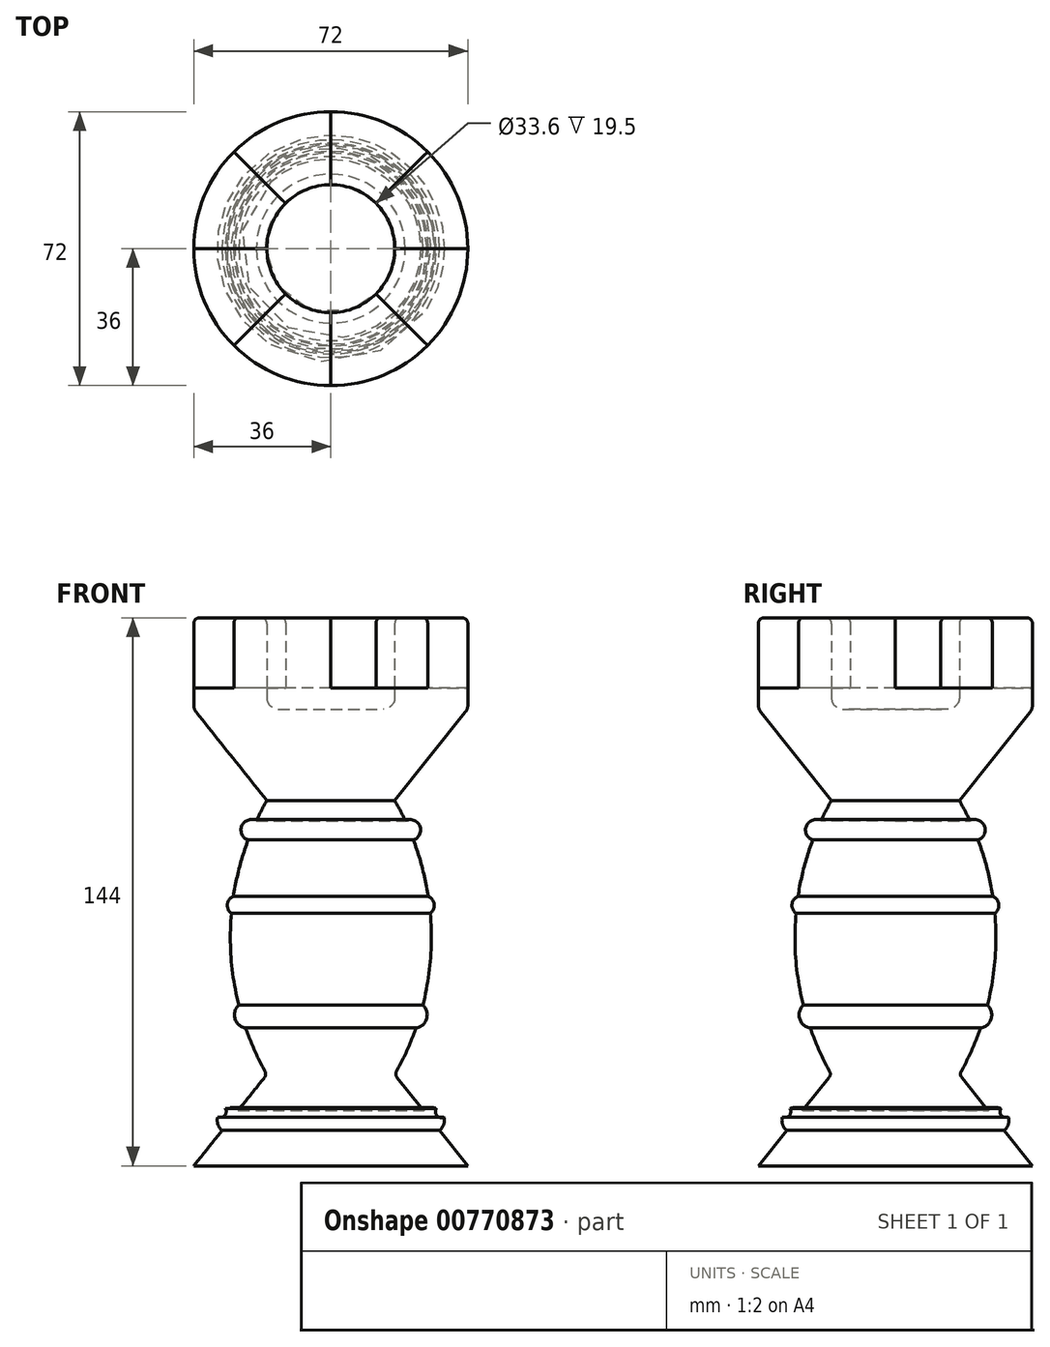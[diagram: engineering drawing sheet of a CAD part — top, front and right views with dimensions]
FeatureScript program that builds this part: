
annotation { "Feature Type Name" : "Feature", "Feature Type Description" : "" }
export const myFeature = defineFeature(function(context is Context, id is Id, definition is map)
    precondition{}
    {
        {
            var Q0;
            Q0=qCreatedBy(makeId("Right.planeOp"),FACE);
            var sketch = newSketch(context, id + "F0", { "sketchPlane" : qUnion([Q0])});
            skLineSegment(sketch, "E0", {"start": v(-36, -74.45) * mm, "end": v(-17.43, -51.25) * mm});
            skLineSegment(sketch, "E1", {"start": v(-35.34, 44.72) * mm, "end": v(-16.8, 21.55) * mm});
            skLineSegment(sketch, "E2", {"start": v(-33, 69.55) * mm, "end": v(-19.8, 69.55) * mm});
            skLineSegment(sketch, "E3", {"start": v(-36, 66.55) * mm, "end": v(-36, 46.6) * mm});
            skLineSegment(sketch, "E4", {"start": v(-16.8, 48.55) * mm, "end": v(-16.8, 66.55) * mm});
            skArc(sketch, "E5", {"start": v(-16.8, 21.55) * mm, "mid": v(-26.4, -13.95) * mm, "end": v(-17.3, -49.58) * mm});
            skLineSegment(sketch, "E6", {"start": v(0, -74.45) * mm, "end": v(-36, -74.45) * mm});
            skLineSegment(sketch, "E7", {"start": v(-13.8, 45.55) * mm, "end": v(0, 45.55) * mm});
            skArc(sketch, "E8", {"start": v(-16.8, 48.55) * mm, "mid": v(-15.92, 46.43) * mm, "end": v(-13.8, 45.55) * mm});
            skArc(sketch, "E9", {"start": v(-36, 46.6) * mm, "mid": v(-35.83, 45.6) * mm, "end": v(-35.34, 44.72) * mm});
            skLineSegment(sketch, "E10", {"start": v(-33, 69.55) * mm, "end": v(-34.5, 69.55) * mm});
            skLineSegment(sketch, "E11", {"start": v(-36, 66.55) * mm, "end": v(-36, 68.05) * mm});
            skLineSegment(sketch, "E12", {"start": v(-19.8, 69.55) * mm, "end": v(-18.3, 69.55) * mm});
            skLineSegment(sketch, "E13", {"start": v(-16.8, 66.55) * mm, "end": v(-16.8, 68.05) * mm});
            skArc(sketch, "E14", {"start": v(-34.5, 69.55) * mm, "mid": v(-35.56, 69.1) * mm, "end": v(-36, 68.05) * mm});
            skArc(sketch, "E15", {"start": v(-16.8, 68.05) * mm, "mid": v(-17.24, 69.1) * mm, "end": v(-18.3, 69.55) * mm});
            skArc(sketch, "E16", {"start": v(-17.43, -51.25) * mm, "mid": v(-17.11, -50.43) * mm, "end": v(-17.3, -49.58) * mm});
            skLineSegment(sketch, "E17", {"start": v(0, -74.45) * mm, "end": v(0, 45.55) * mm});
            skSolve(sketch);
        }
        {
            var Q0;
            Q0=makeQuery(id+"F0.imprint","IMPRINT",FACE,{"disambiguationData":[TD([[makeQuery(id+"F0.imprint","IMPRINT",EDGE,{"derivedFrom":sQuery(id+"F0.wireOp",EDGE,"E0")}),-1.0]])]});
            var Q1;
            Q1=sQuery(id+"F0.wireOp",EDGE,"E17");
            revolve(context, id + "F1", {"surfaceOperationType" : NewSurfaceOperationType.NEW, "entities" : qUnion([Q0]), "axis" : qUnion([Q1]), "revolveType" : RevolveType.FULL});
        }
        {
            var Q0;
            Q0=makeQuery(id+"F1.opRevolve","SWEPT_FACE",FACE,{"disambiguationData":[OSD([sQuery(id+"F0.wireOp",EDGE,"E2"),sQuery(id+"F0.wireOp",EDGE,"E10"),sQuery(id+"F0.wireOp",EDGE,"E12")])]});
            var sketch = newSketch(context, id + "F2", { "sketchPlane" : qUnion([Q0])});
            skLineSegment(sketch, "E18", {"start": v(0, 0) * mm, "end": v(0, 45.62) * mm});
            skLineSegment(sketch, "E19", {"start": v(0, 0) * mm, "end": v(59.77, 0) * mm});
            skLineSegment(sketch, "E20", {"start": v(0, 0) * mm, "end": v(0, -52.46) * mm});
            skLineSegment(sketch, "E21", {"start": v(0, 0) * mm, "end": v(-50.81, 0) * mm});
            skLineSegment(sketch, "E22", {"start": v(0, 0) * mm, "end": v(-38.32, 38.32) * mm});
            skLineSegment(sketch, "E23", {"start": v(0, 0) * mm, "end": v(37.23, 37.23) * mm});
            skLineSegment(sketch, "E24", {"start": v(0, 0) * mm, "end": v(42.66, -42.66) * mm});
            skLineSegment(sketch, "E25", {"start": v(0, 0) * mm, "end": v(-29.95, -29.95) * mm});
            skLineSegment(sketch, "E26", {"start": v(-38.32, 38.32) * mm, "end": v(0, 45.62) * mm});
            skLineSegment(sketch, "E27", {"start": v(37.23, 37.23) * mm, "end": v(59.77, 0) * mm});
            skLineSegment(sketch, "E28", {"start": v(42.66, -42.66) * mm, "end": v(0, -52.46) * mm});
            skLineSegment(sketch, "E29", {"start": v(-29.95, -29.95) * mm, "end": v(-50.81, 0) * mm});
            skSolve(sketch);
        }
        {
            var Q0;
            Q0=qSketchRegion(id+"F2",true);
            extrude(context, id + "F3", {"entities" : qUnion([Q0]), "operationType" : NewBodyOperationType.REMOVE, "oppositeDirection" : true, "depth" : 18.4 * mm, "offsetDistance" : 25 * mm});
        }
        {
            var Q0;
            Q0=qCreatedBy(makeId("Front.planeOp"),FACE);
            var sketch = newSketch(context, id + "F4", { "sketchPlane" : qUnion([Q0])});
            skCircle(sketch, "E30", {"center": v(26.48, -62.5) * mm, "radius": 3.35 * mm});
            skSolve(sketch);
        }
        {
            var Q0;
            Q0=qSketchRegion(id+"F4",true);
            var Q1;
            Q1=makeQuery(id+"F1.opRevolve","SWEPT_FACE",FACE,{"disambiguationData":[OSD([sQuery(id+"F0.wireOp",EDGE,"E0")])]});
            revolve(context, id + "F5", {"operationType" : NewBodyOperationType.ADD, "surfaceOperationType" : NewSurfaceOperationType.NEW, "entities" : qUnion([Q0]), "axis" : qUnion([Q1]), "revolveType" : RevolveType.FULL});
        }
        {
            var Q0;
            Q0=qCreatedBy(makeId("Front.planeOp"),FACE);
            var sketch = newSketch(context, id + "F6", { "sketchPlane" : qUnion([Q0])});
            skCircle(sketch, "E31", {"center": v(29.08, -60.2) * mm, "radius": 1.6 * mm});
            skSolve(sketch);
        }
        {
            var Q0;
            Q0=qSketchRegion(id+"F6",true);
            var Q1;
            Q1=makeQuery(id+"F5.opRevolve","SWEPT_FACE",FACE,{"disambiguationData":[OSD([sQuery(id+"F4.wireOp",EDGE,"E30")])]});
            revolve(context, id + "F7", {"operationType" : NewBodyOperationType.REMOVE, "surfaceOperationType" : NewSurfaceOperationType.NEW, "entities" : qUnion([Q0]), "axis" : qUnion([Q1]), "revolveType" : RevolveType.FULL, "oppositeDirection" : true});
        }
        {
            var Q0;
            Q0=qCreatedBy(makeId("Front.planeOp"),FACE);
            var sketch = newSketch(context, id + "F8", { "sketchPlane" : qUnion([Q0])});
            skCircle(sketch, "E32", {"center": v(20.87, 13.8) * mm, "radius": 2.75 * mm});
            skCircle(sketch, "E33", {"center": v(21.8, -34.78) * mm, "radius": 3.5 * mm});
            skCircle(sketch, "E34", {"center": v(24.64, -6.01) * mm, "radius": 2.55 * mm});
            skSolve(sketch);
        }
        {
            var Q0;
            Q0=qSketchRegion(id+"F8",true);
            var Q1;
            Q1=makeQuery(id+"F1.opRevolve","SWEPT_FACE",FACE,{"disambiguationData":[OSD([sQuery(id+"F0.wireOp",EDGE,"E5")])]});
            revolve(context, id + "F9", {"operationType" : NewBodyOperationType.ADD, "surfaceOperationType" : NewSurfaceOperationType.ADD, "entities" : qUnion([Q0]), "axis" : qUnion([Q1]), "revolveType" : RevolveType.FULL});
        }
    });
